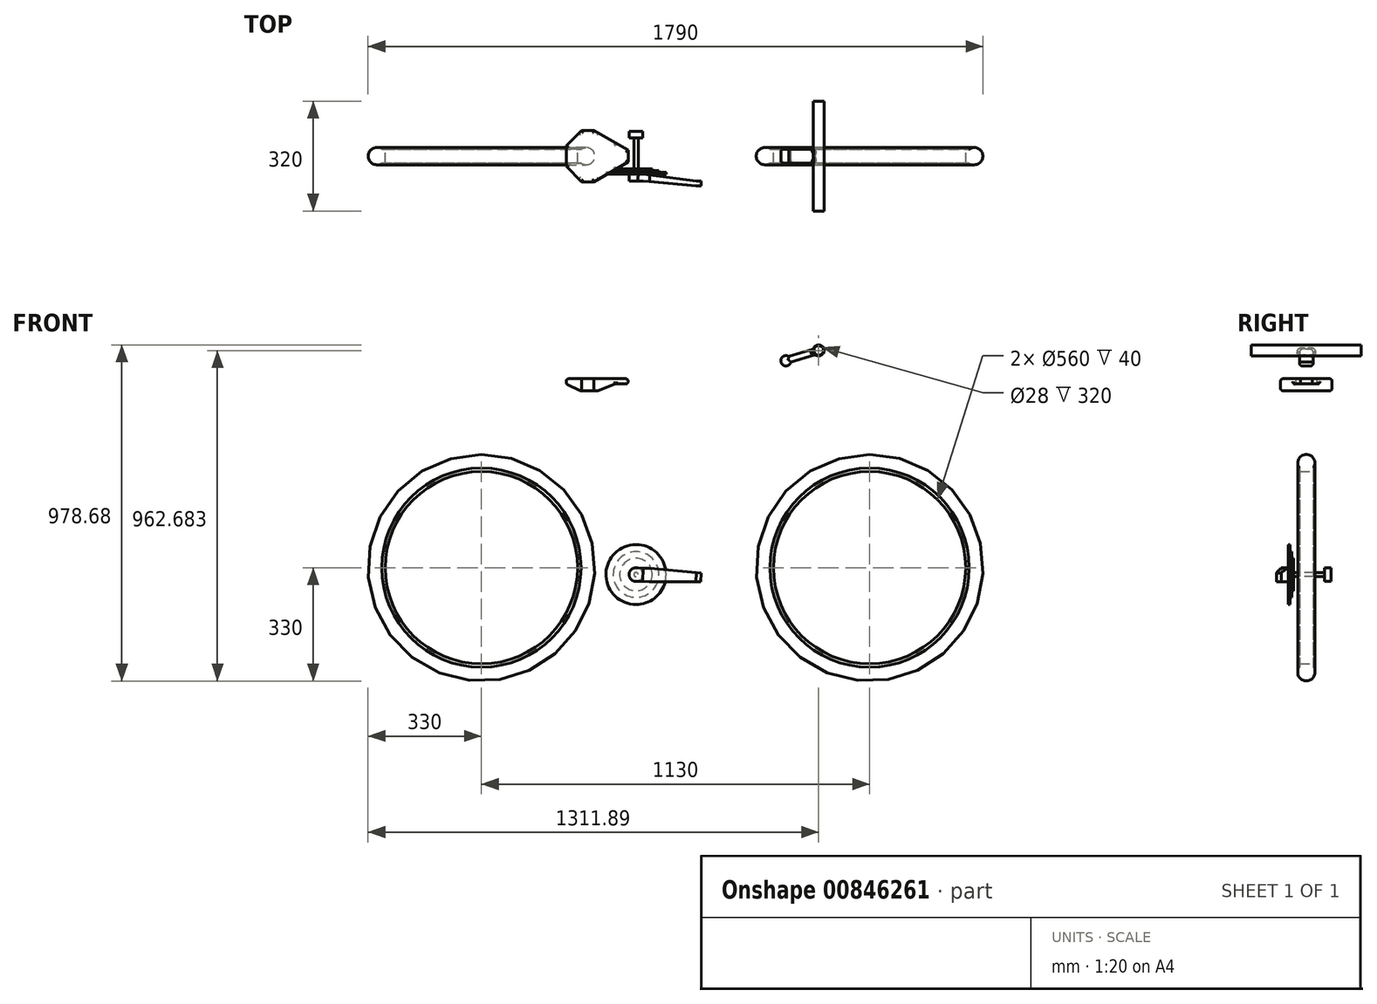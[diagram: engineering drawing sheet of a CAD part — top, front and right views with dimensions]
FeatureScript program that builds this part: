
annotation { "Feature Type Name" : "Feature", "Feature Type Description" : "" }
export const myFeature = defineFeature(function(context is Context, id is Id, definition is map)
    precondition{}
    {
        {
            var Q0;
            Q0=qCreatedBy(makeId("Front.planeOp"),FACE);
            var sketch = newSketch(context, id + "F0", { "sketchPlane" : qUnion([Q0])});
            skLineSegment(sketch, "E0", {"start": v(1130, 0) * mm, "end": v(800, 0) * mm, "construction": true});
            skLineSegment(sketch, "E1", {"start": v(800, 0) * mm, "end": v(450, 0) * mm, "construction": true});
            skLineSegment(sketch, "E2", {"start": v(937.08, 477.5) * mm, "end": v(899.62, 570.22) * mm});
            skLineSegment(sketch, "E3", {"start": v(937.08, 477.5) * mm, "end": v(950.19, 445.05) * mm});
            skLineSegment(sketch, "E4", {"start": v(899.62, 570.22) * mm, "end": v(886.5, 602.67) * mm});
            skLineSegment(sketch, "E5", {"start": v(450, -20) * mm, "end": v(330, -20) * mm, "construction": true});
            skLineSegment(sketch, "E6", {"start": v(330, -20) * mm, "end": v(0, -20) * mm, "construction": true});
            skLineSegment(sketch, "E7", {"start": v(950.19, 445.05) * mm, "end": v(1130, 0) * mm, "construction": true});
            skCircle(sketch, "E8", {"center": v(1130, 0) * mm, "radius": 330 * mm, "construction": true});
            skCircle(sketch, "E9", {"center": v(0, 0) * mm, "radius": 330 * mm, "construction": true});
            skLineSegment(sketch, "E10", {"start": v(450, 0) * mm, "end": v(450, -20) * mm, "construction": true});
            skLineSegment(sketch, "E11", {"start": v(450, -20) * mm, "end": v(0, 0) * mm, "construction": true});
            skLineSegment(sketch, "E12", {"start": v(937.08, 477.5) * mm, "end": v(450, -20) * mm, "construction": true});
            skPoint(sketch, "E13", {"position": v(44.96, -2) * mm});
            skPoint(sketch, "E14", {"position": v(28.87, 34.52) * mm});
            skLineSegment(sketch, "E15", {"start": v(349.46, 370) * mm, "end": v(450, -20) * mm, "construction": true});
            skLineSegment(sketch, "E16", {"start": v(349.46, 370) * mm, "end": v(312.02, 515.25) * mm, "construction": true});
            skPoint(sketch, "E17", {"position": v(309.46, 370) * mm});
            skLineSegment(sketch, "E18", {"start": v(309.46, 370) * mm, "end": v(0, 0) * mm, "construction": true});
            skLineSegment(sketch, "E19", {"start": v(450, 0) * mm, "end": v(0, 0) * mm, "construction": true});
            skLineSegment(sketch, "E20", {"start": v(479.94, -330) * mm, "end": v(-157.99, -330) * mm, "construction": true});
            skCircle(sketch, "E21", {"center": v(450, -20) * mm, "radius": 17 * mm});
            skCircle(sketch, "E22", {"center": v(450, -20) * mm, "radius": 19 * mm});
            skCircle(sketch, "E23", {"center": v(1130, 0) * mm, "radius": 450 * mm, "construction": true});
            skSolve(sketch);
        }
        {
            var Q0;
            Q0=sQuery(id+"F0.wireOp",EDGE,"E11");
            cPlane(context, id + "F1", {"entities" : qUnion([Q0]), "cplaneType" : CPlaneType.LINE_ANGLE, "offset" : 25 * mm, "angle" : 90 * degree, "width" : 150 * mm, "height" : 150 * mm});
        }
        {
            var Q0;
            Q0=qCreatedBy(id+"F1.planeOp",FACE);
            var sketch = newSketch(context, id + "F2", { "sketchPlane" : qUnion([Q0])});
            skLineSegment(sketch, "E24", {"start": v(450.44, -59) * mm, "end": v(450.44, 59) * mm});
            skLineSegment(sketch, "E25.bottom", {"start": v(444.2, 59) * mm, "end": v(456.7, 59) * mm});
            skLineSegment(sketch, "E25.top", {"start": v(444.2, -59) * mm, "end": v(456.7, -59) * mm});
            skLineSegment(sketch, "E25.left", {"start": v(444.2, 59) * mm, "end": v(444.2, -59) * mm});
            skLineSegment(sketch, "E25.right", {"start": v(456.7, 59) * mm, "end": v(456.7, -59) * mm});
            skPoint(sketch, "E25.middle", {"position": v(450.44, 0) * mm});
            skLineSegment(sketch, "E26.bottom", {"start": v(497.94, -42.5) * mm, "end": v(402.94, -42.5) * mm});
            skLineSegment(sketch, "E26.top", {"start": v(497.94, -37.5) * mm, "end": v(402.94, -37.5) * mm});
            skLineSegment(sketch, "E26.left", {"start": v(497.94, -42.5) * mm, "end": v(497.94, -37.5) * mm});
            skLineSegment(sketch, "E26.right", {"start": v(402.94, -42.5) * mm, "end": v(402.94, -37.5) * mm});
            skPoint(sketch, "E26.middle", {"position": v(450.44, -40) * mm});
            skLineSegment(sketch, "E27.bottom", {"start": v(516.94, -47.5) * mm, "end": v(383.94, -47.5) * mm});
            skLineSegment(sketch, "E27.top", {"start": v(516.94, -42.5) * mm, "end": v(383.94, -42.5) * mm});
            skLineSegment(sketch, "E27.left", {"start": v(516.94, -47.5) * mm, "end": v(516.94, -42.5) * mm});
            skLineSegment(sketch, "E27.right", {"start": v(383.94, -47.5) * mm, "end": v(383.94, -42.5) * mm});
            skPoint(sketch, "E27.middle", {"position": v(450.44, -45) * mm});
            skLineSegment(sketch, "E28.bottom", {"start": v(537.94, -52.5) * mm, "end": v(362.94, -52.5) * mm});
            skLineSegment(sketch, "E28.top", {"start": v(537.94, -47.5) * mm, "end": v(362.94, -47.5) * mm});
            skLineSegment(sketch, "E28.left", {"start": v(537.94, -52.5) * mm, "end": v(537.94, -47.5) * mm});
            skLineSegment(sketch, "E28.right", {"start": v(362.94, -52.5) * mm, "end": v(362.94, -47.5) * mm});
            skPoint(sketch, "E28.middle", {"position": v(450.44, -50) * mm});
            skLineSegment(sketch, "E29.bottom", {"start": v(470.44, -72.5) * mm, "end": v(430.44, -72.5) * mm});
            skLineSegment(sketch, "E29.top", {"start": v(470.44, -52.5) * mm, "end": v(430.44, -52.5) * mm});
            skLineSegment(sketch, "E29.left", {"start": v(470.44, -72.5) * mm, "end": v(470.44, -52.5) * mm});
            skLineSegment(sketch, "E29.right", {"start": v(430.44, -72.5) * mm, "end": v(430.44, -52.5) * mm});
            skPoint(sketch, "E29.middle", {"position": v(450.44, -62.5) * mm});
            skLineSegment(sketch, "E30.bottom", {"start": v(639.44, -86.5) * mm, "end": v(625.44, -86.5) * mm});
            skLineSegment(sketch, "E30.top", {"start": v(639.44, -72.5) * mm, "end": v(625.44, -72.5) * mm});
            skLineSegment(sketch, "E30.left", {"start": v(639.44, -86.5) * mm, "end": v(639.44, -72.5) * mm});
            skLineSegment(sketch, "E30.right", {"start": v(625.44, -86.5) * mm, "end": v(625.44, -72.5) * mm});
            skPoint(sketch, "E30.middle", {"position": v(632.44, -79.5) * mm});
            skLineSegment(sketch, "E31", {"start": v(450.44, -59) * mm, "end": v(450.44, -164.84) * mm});
            skLineSegment(sketch, "E32", {"start": v(470.44, -72.5) * mm, "end": v(625.44, -72.5) * mm, "construction": true});
            skLineSegment(sketch, "E33", {"start": v(625.44, -86.5) * mm, "end": v(470.44, -72.5) * mm});
            skLineSegment(sketch, "E34", {"start": v(625.44, -72.5) * mm, "end": v(470.44, -52.5) * mm});
            skLineSegment(sketch, "E35.MirrorCS", {"start": v(430.44, 72.5) * mm, "end": v(430.44, 52.5) * mm});
            skLineSegment(sketch, "E36.MirrorCS", {"start": v(470.44, 52.5) * mm, "end": v(430.44, 52.5) * mm});
            skLineSegment(sketch, "E37.MirrorCS", {"start": v(470.44, 72.5) * mm, "end": v(430.44, 72.5) * mm});
            skLineSegment(sketch, "E38.MirrorCS", {"start": v(625.44, 72.5) * mm, "end": v(470.44, 52.5) * mm});
            skLineSegment(sketch, "E39.MirrorCS", {"start": v(625.44, 86.5) * mm, "end": v(470.44, 72.5) * mm});
            skLineSegment(sketch, "E40.MirrorCS", {"start": v(639.44, 86.5) * mm, "end": v(625.44, 86.5) * mm});
            skLineSegment(sketch, "E41.MirrorCS", {"start": v(639.44, 86.5) * mm, "end": v(639.44, 72.5) * mm});
            skLineSegment(sketch, "E42.MirrorCS", {"start": v(639.44, 72.5) * mm, "end": v(625.44, 72.5) * mm});
            skLineSegment(sketch, "E43.MirrorCS", {"start": v(450.44, 59) * mm, "end": v(450.44, 164.84) * mm});
            skLineSegment(sketch, "E44.MirrorCS", {"start": v(470.44, 72.5) * mm, "end": v(470.44, 52.5) * mm});
            skSolve(sketch);
        }
        {
            var Q0;
            Q0=qCreatedBy(makeId("Front.planeOp"),FACE);
            var sketch = newSketch(context, id + "F3", { "sketchPlane" : qUnion([Q0])});
            skLineSegment(sketch, "E45", {"start": v(287.02, 515.25) * mm, "end": v(312.02, 515.25) * mm});
            skLineSegment(sketch, "E46", {"start": v(312.02, 515.25) * mm, "end": v(337.02, 515.25) * mm});
            skLineSegment(sketch, "E47", {"start": v(337.02, 515.25) * mm, "end": v(388.24, 535.25) * mm});
            skLineSegment(sketch, "E48", {"start": v(388.24, 535.25) * mm, "end": v(427.02, 535.25) * mm});
            skLineSegment(sketch, "E49", {"start": v(427.02, 535.25) * mm, "end": v(427.02, 550.25) * mm});
            skLineSegment(sketch, "E50", {"start": v(427.02, 550.25) * mm, "end": v(337.02, 550.25) * mm});
            skLineSegment(sketch, "E51", {"start": v(337.02, 550.25) * mm, "end": v(247.02, 550.25) * mm});
            skLineSegment(sketch, "E52", {"start": v(247.02, 550.25) * mm, "end": v(247.02, 535.25) * mm});
            skLineSegment(sketch, "E53", {"start": v(247.02, 535.25) * mm, "end": v(287.02, 515.25) * mm});
            skLineSegment(sketch, "E54", {"start": v(337.02, 515.25) * mm, "end": v(337.02, 550.25) * mm, "construction": true});
            skLineSegment(sketch, "E55", {"start": v(247.02, 535.25) * mm, "end": v(337.02, 535.25) * mm, "construction": true});
            skSolve(sketch);
        }
        {
            var Q0;
            Q0=qCreatedBy(makeId("Front.planeOp"),FACE);
            var sketch = newSketch(context, id + "F4", { "sketchPlane" : qUnion([Q0])});
            skLineSegment(sketch, "E56", {"start": v(886.5, 602.67) * mm, "end": v(981.9, 632.68) * mm, "construction": true});
            skLineSegment(sketch, "E57", {"start": v(981.9, 632.68) * mm, "end": v(981.9, 602.67) * mm, "construction": true});
            skLineSegment(sketch, "E58", {"start": v(981.9, 602.67) * mm, "end": v(886.5, 602.67) * mm, "construction": true});
            skCircle(sketch, "E59", {"center": v(981.9, 632.68) * mm, "radius": 14 * mm});
            skCircle(sketch, "E60", {"center": v(981.9, 632.68) * mm, "radius": 16 * mm});
            skLineSegment(sketch, "E61", {"start": v(966.65, 637.55) * mm, "end": v(895.03, 615.02) * mm});
            skLineSegment(sketch, "E62", {"start": v(895.03, 615.02) * mm, "end": v(900.11, 598.85) * mm, "construction": true});
            skLineSegment(sketch, "E63", {"start": v(900.11, 598.85) * mm, "end": v(972.19, 619.96) * mm});
            skLineSegment(sketch, "E64", {"start": v(972.19, 619.96) * mm, "end": v(966.65, 637.55) * mm, "construction": true});
            skCircle(sketch, "E65", {"center": v(886.5, 602.67) * mm, "radius": 15 * mm});
            skSolve(sketch);
        }
        {
            var Q0;
            Q0=qCreatedBy(makeId("Top.planeOp"),FACE);
            var sketch = newSketch(context, id + "F5", { "sketchPlane" : qUnion([Q0])});
            skLineSegment(sketch, "E66.bottom", {"start": v(280, 20) * mm, "end": v(290, 20) * mm});
            skLineSegment(sketch, "E66.top", {"start": v(280, -20) * mm, "end": v(290, -20) * mm});
            skLineSegment(sketch, "E66.left", {"start": v(280, 20) * mm, "end": v(280, -20) * mm});
            skLineSegment(sketch, "E66.right", {"start": v(290, 20) * mm, "end": v(290, -20) * mm});
            skArc(sketch, "E67", {"start": v(290, -20) * mm, "mid": v(330, 0) * mm, "end": v(290, 20) * mm});
            skLineSegment(sketch, "E68.bottom", {"start": v(1410, 20) * mm, "end": v(1420, 20) * mm});
            skLineSegment(sketch, "E68.top", {"start": v(1410, -20) * mm, "end": v(1420, -20) * mm});
            skLineSegment(sketch, "E68.left", {"start": v(1410, 20) * mm, "end": v(1410, -20) * mm});
            skLineSegment(sketch, "E68.right", {"start": v(1420, 20) * mm, "end": v(1420, -20) * mm});
            skArc(sketch, "E69", {"start": v(1420, -20) * mm, "mid": v(1460, 0) * mm, "end": v(1420, 20) * mm});
            skSolve(sketch);
        }
        {
            var Q0;
            Q0=makeQuery(id+"F5.imprint","IMPRINT",FACE,{"disambiguationData":[TD([[makeQuery(id+"F5.imprint","IMPRINT",EDGE,{"derivedFrom":sQuery(id+"F5.wireOp",EDGE,"E66.bottom")}),-1.0]])]});
            var Q1;
            Q1=makeQuery(id+"F5.imprint","IMPRINT",FACE,{"disambiguationData":[TD([[makeQuery(id+"F5.imprint","IMPRINT",EDGE,{"derivedFrom":sQuery(id+"F5.wireOp",EDGE,"E66.right")}),1.0]])]});
            var Q2;
            Q2=sQuery(id+"F0.wireOp",EDGE,"E9");
            revolve(context, id + "F6", {"surfaceOperationType" : NewSurfaceOperationType.NEW, "entities" : qUnion([Q0, Q1]), "axis" : qUnion([Q2]), "revolveType" : RevolveType.FULL});
        }
        {
            var Q0;
            Q0=makeQuery(id+"F5.imprint","IMPRINT",FACE,{"disambiguationData":[TD([[makeQuery(id+"F5.imprint","IMPRINT",EDGE,{"derivedFrom":sQuery(id+"F5.wireOp",EDGE,"E68.right")}),1.0]])]});
            var Q1;
            Q1=makeQuery(id+"F5.imprint","IMPRINT",FACE,{"disambiguationData":[TD([[makeQuery(id+"F5.imprint","IMPRINT",EDGE,{"derivedFrom":sQuery(id+"F5.wireOp",EDGE,"E68.bottom")}),-1.0]])]});
            var Q2;
            Q2=sQuery(id+"F0.wireOp",EDGE,"E8");
            revolve(context, id + "F7", {"surfaceOperationType" : NewSurfaceOperationType.NEW, "entities" : qUnion([Q0, Q1]), "axis" : qUnion([Q2]), "revolveType" : RevolveType.FULL});
        }
        {
            var Q0;
            Q0=makeQuery(id+"F4.imprint","IMPRINT",FACE,{"disambiguationData":[TD([[makeQuery(id+"F4.imprint","IMPRINT",EDGE,{"derivedFrom":sQuery(id+"F4.wireOp",EDGE,"E59")}),-1.0]])]});
            extrude(context, id + "F8", {"entities" : qUnion([Q0]), "endBound" : BoundingType.SYMMETRIC, "depth" : 320 * mm, "offsetDistance" : 25 * mm});
        }
        {
            var Q0;
            {var subQ0=sQuery(id+"F4.wireOp",EDGE,"E65");var subQ1=makeQuery(id+"F4.imprint","INTERSECT",VERTEX,{"derivedFrom":[sQuery(id+"F4.wireOp",EDGE,"E61"),subQ0]});Q0=makeQuery(id+"F4.imprint","IMPRINT",FACE,{"disambiguationData":[TD([[makeQuery(id+"F4.imprint","IMPRINT",EDGE,{"disambiguationData":[TD([[subQ1,-1.0]])],"derivedFrom":subQ0}),1.0]])]});}
            var Q1;
            {var subQ0=sQuery(id+"F4.wireOp",EDGE,"E61");Q1=makeQuery(id+"F4.imprint","IMPRINT",FACE,{"disambiguationData":[TD([[makeQuery(id+"F4.imprint","IMPRINT",EDGE,{"derivedFrom":subQ0}),1.0]])]});}
            extrude(context, id + "F9", {"entities" : qUnion([Q0, Q1]), "operationType" : NewBodyOperationType.ADD, "endBound" : BoundingType.SYMMETRIC, "depth" : 40 * mm, "offsetDistance" : 25 * mm});
        }
        {
            var Q0;
            Q0=makeQuery(id+"F9.opExtrude","CAP_FACE",FACE,{"disambiguationData":[OSD([sQuery(id+"F4.wireOp",EDGE,"E60"),sQuery(id+"F4.wireOp",EDGE,"E61"),sQuery(id+"F4.wireOp",EDGE,"E63"),sQuery(id+"F4.wireOp",EDGE,"E65")])],"isStart":false});
            var Q1;
            Q1=makeQuery(id+"F9.opExtrude","CAP_FACE",FACE,{"disambiguationData":[OSD([sQuery(id+"F4.wireOp",EDGE,"E60"),sQuery(id+"F4.wireOp",EDGE,"E61"),sQuery(id+"F4.wireOp",EDGE,"E63"),sQuery(id+"F4.wireOp",EDGE,"E65")])],"isStart":true});
            fillet(context, id + "F10", {"entities" : qUnion([Q0, Q1]), "radius" : 8 * mm, "tangentPropagation" : true, "allowEdgeOverflow" : false});
        }
        {
            var Q0;
            Q0=makeQuery(id+"F3.imprint","IMPRINT",FACE,{"disambiguationData":[TD([[makeQuery(id+"F3.imprint","IMPRINT",EDGE,{"derivedFrom":sQuery(id+"F3.wireOp",EDGE,"E45")}),1.0]])]});
            extrude(context, id + "F11", {"entities" : qUnion([Q0]), "endBound" : BoundingType.SYMMETRIC, "depth" : 150 * mm, "offsetDistance" : 25 * mm});
        }
        {
            var Q0;
            Q0=makeQuery(id+"F11.opExtrude","CAP_EDGE",EDGE,{"disambiguationData":[OSD([sQuery(id+"F3.wireOp",EDGE,"E49")])],"isStart":false});
            var Q1;
            Q1=makeQuery(id+"F11.opExtrude","CAP_EDGE",EDGE,{"disambiguationData":[OSD([sQuery(id+"F3.wireOp",EDGE,"E49")])],"isStart":true});
            chamfer(context, id + "F12", {"entities" : qUnion([Q0, Q1]), "chamferType" : ChamferType.OFFSET_ANGLE, "width" : 100 * mm, "oppositeDirection" : false, "angle" : 30 * degree});
        }
        {
            var Q0;
            Q0=makeQuery(id+"F11.opExtrude","CAP_EDGE",EDGE,{"disambiguationData":[OSD([sQuery(id+"F3.wireOp",EDGE,"E52")])],"isStart":true});
            var Q1;
            Q1=makeQuery(id+"F11.opExtrude","CAP_EDGE",EDGE,{"disambiguationData":[OSD([sQuery(id+"F3.wireOp",EDGE,"E52")])],"isStart":false});
            chamfer(context, id + "F13", {"entities" : qUnion([Q0, Q1]), "width" : 45 * mm, "tangentPropagation" : true});
        }
        {
            var Q0;
            Q0=makeQuery(id+"F11.opExtrude","SWEPT_FACE",FACE,{"disambiguationData":[OSD([sQuery(id+"F3.wireOp",EDGE,"E50"),sQuery(id+"F3.wireOp",EDGE,"E51")])]});
            var Q1;
            Q1=makeQuery(id+"F11.opExtrude","SWEPT_FACE",FACE,{"disambiguationData":[OSD([sQuery(id+"F3.wireOp",EDGE,"E53")])]});
            var Q2;
            Q2=makeQuery(id+"F11.opExtrude","SWEPT_FACE",FACE,{"disambiguationData":[OSD([sQuery(id+"F3.wireOp",EDGE,"E45"),sQuery(id+"F3.wireOp",EDGE,"E46")])]});
            var Q3;
            Q3=makeQuery(id+"F11.opExtrude","SWEPT_FACE",FACE,{"disambiguationData":[OSD([sQuery(id+"F3.wireOp",EDGE,"E48")])]});
            var Q4;
            Q4=makeQuery(id+"F11.opExtrude","SWEPT_FACE",FACE,{"disambiguationData":[OSD([sQuery(id+"F3.wireOp",EDGE,"E47")])]});
            fillet(context, id + "F14", {"entities" : qUnion([Q0, Q1, Q2, Q3, Q4]), "radius" : 7 * mm, "tangentPropagation" : true, "allowEdgeOverflow" : false});
        }
        {
            var Q0;
            {var subQ3=sQuery(id+"F2.wireOp",EDGE,"E36.MirrorCS");var subQ5=sQuery(id+"F2.wireOp",EDGE,"E25.left");var subQ7=makeQuery(id+"F2.imprint","INTERSECT",VERTEX,{"derivedFrom":[subQ5,subQ3]});Q0=makeQuery(id+"F2.imprint","IMPRINT",FACE,{"disambiguationData":[TD([[makeQuery(id+"F2.imprint","IMPRINT",EDGE,{"disambiguationData":[TD([[subQ7,1.0]])],"derivedFrom":subQ5}),1.0]])]});}
            var Q1;
            {var subQ0=sQuery(id+"F2.wireOp",EDGE,"E26.top");var subQ1=sQuery(id+"F2.wireOp",EDGE,"E24");var subQ2=makeQuery(id+"F2.imprint","INTERSECT",VERTEX,{"derivedFrom":[subQ1,subQ0]});Q1=makeQuery(id+"F2.imprint","IMPRINT",FACE,{"disambiguationData":[TD([[makeQuery(id+"F2.imprint","IMPRINT",EDGE,{"disambiguationData":[TD([[subQ2,1.0]])],"derivedFrom":subQ1}),1.0]])]});}
            var Q2;
            {var subQ0=sQuery(id+"F2.wireOp",EDGE,"E27.bottom");var subQ1=sQuery(id+"F2.wireOp",EDGE,"E24");var subQ2=makeQuery(id+"F2.imprint","INTERSECT",VERTEX,{"derivedFrom":[subQ1,subQ0]});Q2=makeQuery(id+"F2.imprint","IMPRINT",FACE,{"disambiguationData":[TD([[makeQuery(id+"F2.imprint","IMPRINT",EDGE,{"disambiguationData":[TD([[subQ2,-1.0]])],"derivedFrom":subQ1}),1.0]])]});}
            var Q3;
            {var subQ0=sQuery(id+"F2.wireOp",EDGE,"E27.bottom");var subQ1=sQuery(id+"F2.wireOp",EDGE,"E24");var subQ2=makeQuery(id+"F2.imprint","INTERSECT",VERTEX,{"derivedFrom":[subQ1,subQ0]});Q3=makeQuery(id+"F2.imprint","IMPRINT",FACE,{"disambiguationData":[TD([[makeQuery(id+"F2.imprint","IMPRINT",EDGE,{"disambiguationData":[TD([[subQ2,1.0]])],"derivedFrom":subQ1}),1.0]])]});}
            var Q4;
            {var subQ3=sQuery(id+"F2.wireOp",EDGE,"E28.bottom");var subQ5=sQuery(id+"F2.wireOp",EDGE,"E25.left");var subQ7=makeQuery(id+"F2.imprint","INTERSECT",VERTEX,{"derivedFrom":[subQ5,subQ3]});Q4=makeQuery(id+"F2.imprint","IMPRINT",FACE,{"disambiguationData":[TD([[makeQuery(id+"F2.imprint","IMPRINT",EDGE,{"disambiguationData":[TD([[subQ7,-1.0]])],"derivedFrom":subQ5}),1.0]])]});}
            var Q5;
            {var subQ5=sQuery(id+"F2.wireOp",EDGE,"E26.right");Q5=makeQuery(id+"F2.imprint","IMPRINT",FACE,{"disambiguationData":[TD([[makeQuery(id+"F2.imprint","IMPRINT",EDGE,{"derivedFrom":subQ5}),-1.0]])]});}
            var Q6;
            {var subQ3=sQuery(id+"F2.wireOp",EDGE,"E27.right");Q6=makeQuery(id+"F2.imprint","IMPRINT",FACE,{"disambiguationData":[TD([[makeQuery(id+"F2.imprint","IMPRINT",EDGE,{"derivedFrom":subQ3}),-1.0]])]});}
            var Q7;
            {var subQ8=sQuery(id+"F2.wireOp",EDGE,"E28.right");Q7=makeQuery(id+"F2.imprint","IMPRINT",FACE,{"disambiguationData":[TD([[makeQuery(id+"F2.imprint","IMPRINT",EDGE,{"derivedFrom":subQ8}),-1.0]])]});}
            var Q8;
            {var subQ3=sQuery(id+"F2.wireOp",EDGE,"E29.right");Q8=makeQuery(id+"F2.imprint","IMPRINT",FACE,{"disambiguationData":[TD([[makeQuery(id+"F2.imprint","IMPRINT",EDGE,{"derivedFrom":subQ3}),-1.0]])]});}
            var Q9;
            {var subQ0=sQuery(id+"F2.wireOp",EDGE,"E26.top");var subQ1=sQuery(id+"F2.wireOp",EDGE,"E24");var subQ2=makeQuery(id+"F2.imprint","INTERSECT",VERTEX,{"derivedFrom":[subQ1,subQ0]});Q9=makeQuery(id+"F2.imprint","IMPRINT",FACE,{"disambiguationData":[TD([[makeQuery(id+"F2.imprint","IMPRINT",EDGE,{"disambiguationData":[TD([[subQ2,-1.0]])],"derivedFrom":subQ1}),1.0]])]});}
            var Q10;
            {var subQ0=sQuery(id+"F2.wireOp",EDGE,"E35.MirrorCS");Q10=makeQuery(id+"F2.imprint","IMPRINT",FACE,{"disambiguationData":[TD([[makeQuery(id+"F2.imprint","IMPRINT",EDGE,{"derivedFrom":subQ0}),1.0]])]});}
            var Q11;
            Q11=sQuery(id+"F2.wireOp",EDGE,"E24");
            revolve(context, id + "F15", {"surfaceOperationType" : NewSurfaceOperationType.NEW, "entities" : qUnion([Q0, Q1, Q2, Q3, Q4, Q5, Q6, Q7, Q8, Q9, Q10]), "axis" : qUnion([Q11]), "revolveType" : RevolveType.FULL});
        }
        {
            var Q0;
            {var subQ3=sQuery(id+"F2.wireOp",EDGE,"E29.left");Q0=makeQuery(id+"F2.imprint","IMPRINT",FACE,{"disambiguationData":[TD([[makeQuery(id+"F2.imprint","IMPRINT",EDGE,{"derivedFrom":subQ3}),1.0]])]});}
            var Q1;
            Q1=makeQuery(id+"F2.imprint","IMPRINT",FACE,{"disambiguationData":[TD([[makeQuery(id+"F2.imprint","IMPRINT",EDGE,{"derivedFrom":sQuery(id+"F2.wireOp",EDGE,"E29.left")}),-1.0]])]});
            var Q2;
            Q2=makeQuery(id+"F2.imprint","IMPRINT",FACE,{"disambiguationData":[TD([[makeQuery(id+"F2.imprint","IMPRINT",EDGE,{"derivedFrom":sQuery(id+"F2.wireOp",EDGE,"E30.bottom")}),-1.0]])]});
            extrude(context, id + "F16", {"entities" : qUnion([Q0, Q1, Q2]), "operationType" : NewBodyOperationType.ADD, "endBound" : BoundingType.SYMMETRIC, "depth" : 39 * mm, "offsetDistance" : 25 * mm});
        }
        {
            var Q0;
            Q0=makeQuery(id+"F16.opExtrude","CAP_EDGE",EDGE,{"disambiguationData":[OSD([sQuery(id+"F2.wireOp",EDGE,"E30.left")])],"isStart":false});
            var Q1;
            Q1=makeQuery(id+"F16.opExtrude","CAP_EDGE",EDGE,{"disambiguationData":[OSD([sQuery(id+"F2.wireOp",EDGE,"E30.left")])],"isStart":true});
            chamfer(context, id + "F17", {"entities" : qUnion([Q0, Q1]), "chamferType" : ChamferType.TWO_OFFSETS, "width1" : 150 * mm, "oppositeDirection" : false, "width2" : 7 * mm});
        }
    });
